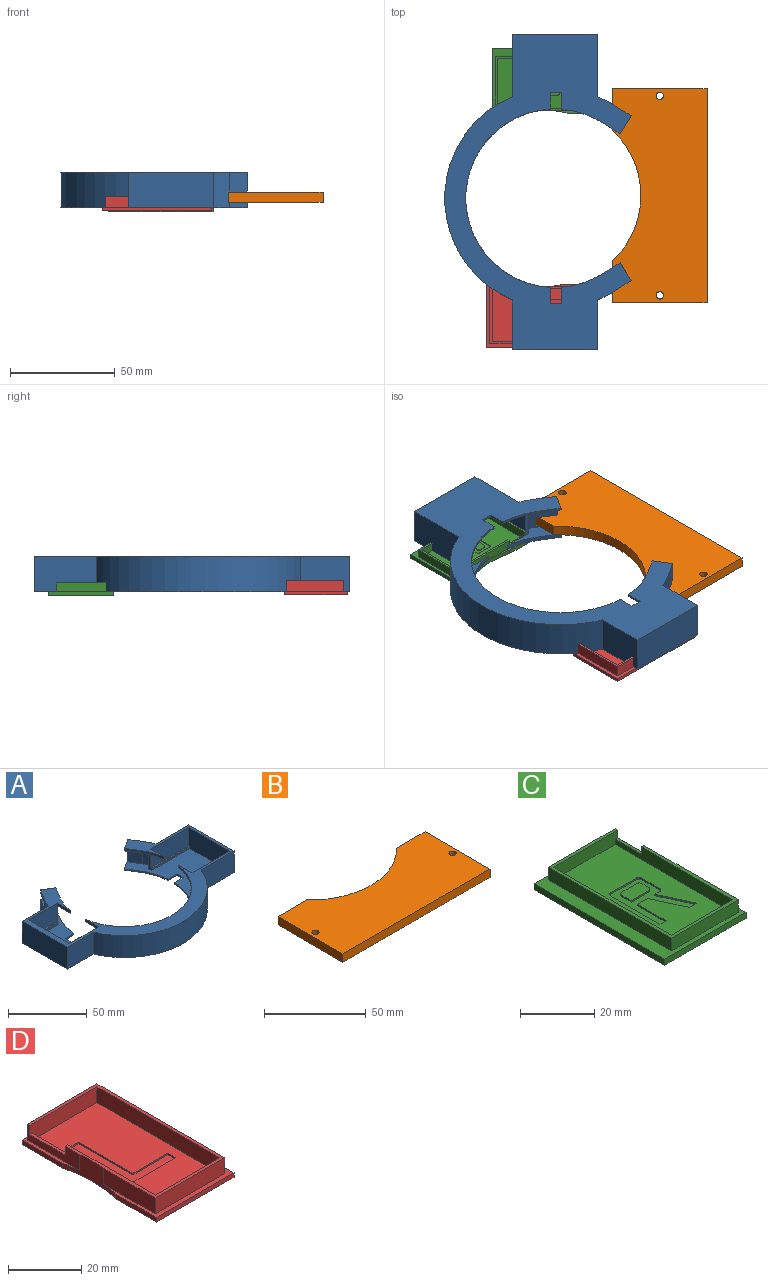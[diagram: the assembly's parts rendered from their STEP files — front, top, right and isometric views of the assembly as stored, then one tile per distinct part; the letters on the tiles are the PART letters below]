
ASSEMBLY  parts=4 mates=3
PART A: 78 faces, bbox 150x88.8x17 mm
  f0: plane 144x85.74mm, normal (0,0,1), area 3182.5mm2, adj f2,f6,f8,f10,f11,f12,f13,f14
  f1: plane 34x14.5mm, normal (0,1,0), area 493mm2, adj f18,f19,f45,f46,f75
  f2: plane 37x16mm, normal (1,0,0), area 589mm2, adj f0,f3,f18,f43,f70,f71,f72,f73
  f3: plane 26x14.5mm, normal (0,1,0), area 377mm2, adj f2,f13,f18,f42,f73
  f4: plane 8.48x5.3mm, normal (-0.85,0.53,0), area 25mm2, adj f7,f18,f24,f69
  f5: cylinder r=52.5mm len=17mm, axis (0,0,1), area 142.6mm2, adj f9,f18,f28,f39,f62,f64,f65,f66
  f6: plane 8.5x8.48mm, normal (0.85,-0.53,0), area 85mm2, adj f0,f23,f58,f67
  f7: plane 8.48x5.3mm, normal (0.53,0.85,0), area 21mm2, adj f4,f18,f25,f56,f57,f69
  f8: plane 8.5x8.48mm, normal (-0.85,-0.53,0), area 85mm2, adj f0,f10,f26,f65
  f9: plane 9.5x8.48mm, normal (0.85,0.53,0), area 95mm2, adj f5,f10,f28,f65
  f10: plane 9.5x8.48mm, normal (-0.53,0.85,0), area 27mm2, adj f0,f8,f9,f28,f59,f65
  f11: cylinder r=42.5mm len=19.27mm, axis (0,0,1), area 20.5mm2, adj f0,f28,f53,f59
  f12: cylinder r=42.5mm len=84.88mm, axis (0,0,1), area 129mm2, adj f0,f28,f49,f51
  f13: plane 14x2.75mm, normal (1,0,0), area 26mm2, adj f0,f3,f29,f31,f72,f73
  f14: plane 14x2.75mm, normal (-1,0,0), area 26mm2, adj f0,f22,f36,f47,f76,f77
  f15: cylinder r=42.5mm len=16.02mm, axis (0,0,1), area 34.4mm2, adj f18,f22,f44,f61
  f16: cylinder r=42.5mm len=19.27mm, axis (0,0,1), area 20.5mm2, adj f0,f28,f50,f54
  f17: cylinder r=42.5mm len=84mm, axis (0,0,1), area 240.9mm2, adj f18,f29,f42,f45
  f18: plane 150x88.8mm, normal (0,0,1), area 1941.9mm2, adj f1,f2,f3,f4,f5,f7,f15,f17
  f19: plane 14x2.75mm, normal (-1,0,0), area 26mm2, adj f0,f1,f29,f37,f74,f75
  f20: cylinder r=50.5mm len=92.52mm, axis (0,0,1), area 1637.7mm2, adj f0,f29,f31,f37
  f21: cylinder r=52.5mm len=96.88mm, axis (0,0,1), area 2097mm2, adj f18,f28,f34,f38
  f22: plane 28.74x15.52mm, normal (0,0,-1), area 145.9mm2, adj f14,f15,f26,f36,f44,f60,f61,f63
  f23: cylinder r=50.5mm len=14mm, axis (0,0,1), area 103.2mm2, adj f0,f6,f25,f32,f57,f68
  f24: cylinder r=52.5mm len=17mm, axis (0,0,1), area 145.1mm2, adj f4,f18,f28,f33,f55,f68
  f25: plane 28.74x15.52mm, normal (0,0,-1), area 145.9mm2, adj f7,f23,f27,f30,f32,f41,f56,f57
  f26: cylinder r=50.5mm len=14mm, axis (0,0,1), area 100.7mm2, adj f0,f8,f22,f36,f60,f64,f65,f66
  f27: cylinder r=42.5mm len=16.02mm, axis (0,0,1), area 34.4mm2, adj f18,f25,f41,f56
  f28: plane 150x88.8mm, normal (0,0,-1), area 4067.7mm2, adj f5,f9,f10,f11,f12,f16,f21,f24
  f29: plane 92.52x44mm, normal (0,0,-1), area 885mm2, adj f13,f17,f19,f20,f31,f37,f42,f45
  f30: plane 14x2.75mm, normal (1,0,0), area 26mm2, adj f0,f25,f32,f43,f70,f71
  f31: plane 14x4.26mm, normal (0,-1,0), area 59.7mm2, adj f0,f13,f20,f29
  f32: plane 14x4.26mm, normal (0,1,0), area 59.7mm2, adj f0,f23,f25,f30
  f33: plane 23.56x17mm, normal (0,1,0), area 400.6mm2, adj f18,f24,f28,f35
  f34: plane 23.56x17mm, normal (0,-1,0), area 400.6mm2, adj f18,f21,f28,f35
  f35: plane 40.5x17mm, normal (-1,0,0), area 688.5mm2, adj f18,f28,f33,f34
  f36: plane 14x4.26mm, normal (0,1,0), area 59.7mm2, adj f0,f14,f22,f26
  f37: plane 14x4.26mm, normal (0,-1,0), area 59.7mm2, adj f0,f19,f20,f29
  f38: plane 29.56x17mm, normal (0,-1,0), area 502.6mm2, adj f18,f21,f28,f40
  f39: plane 29.56x17mm, normal (0,1,0), area 502.6mm2, adj f5,f18,f28,f40
  f40: plane 40.5x17mm, normal (1,0,0), area 688.5mm2, adj f18,f28,f38,f39
  f41: plane 12x2mm, normal (-1,0,0), area 24mm2, adj f18,f25,f27,f43
  f42: plane 12x2mm, normal (-1,0,0), area 24mm2, adj f3,f17,f18,f29
  f43: plane 26x14.5mm, normal (0,-1,0), area 377mm2, adj f2,f18,f30,f41,f71
  f44: plane 12x2mm, normal (1,0,0), area 24mm2, adj f15,f18,f22,f47
  f45: plane 12x2mm, normal (1,0,0), area 24mm2, adj f1,f17,f18,f29
  f46: plane 37x16mm, normal (-1,0,0), area 589mm2, adj f0,f1,f18,f47,f74,f75,f76,f77
  f47: plane 34x14.5mm, normal (0,-1,0), area 493mm2, adj f14,f18,f44,f46,f77
  f48: plane 5.5x1mm, normal (1,0,0), area 5.5mm2, adj f0,f28,f49,f50
  f49: plane 7.78x1mm, normal (0,1,0), area 7.8mm2, adj f0,f12,f28,f48
  f50: plane 7.85x1mm, normal (0,-1,0), area 7.8mm2, adj f0,f16,f28,f48
  f51: plane 7.84x1mm, normal (0,1,0), area 7.8mm2, adj f0,f12,f28,f52
  f52: plane 5.5x1mm, normal (-1,0,0), area 5.5mm2, adj f0,f28,f51,f53
  f53: plane 7.9x1mm, normal (0,-1,0), area 7.9mm2, adj f0,f11,f28,f52
  f54: plane 8.48x5.3mm, normal (0.85,-0.53,0), area 10mm2, adj f0,f16,f28,f58
  f55: plane 9.5x8.48mm, normal (-0.85,0.53,0), area 95mm2, adj f24,f28,f58,f67
  f56: plane 8.48x5.3mm, normal (0.85,-0.53,0), area 20mm2, adj f7,f18,f25,f27
  f57: plane 8.48x5.3mm, normal (0.85,-0.53,0), area 5mm2, adj f7,f23,f25,f69
  f58: plane 9.5x8.48mm, normal (0.53,0.85,0), area 27mm2, adj f0,f6,f28,f54,f55,f67
  f59: plane 8.48x5.3mm, normal (-0.85,-0.53,0), area 10mm2, adj f0,f10,f11,f28
  f60: plane 8.48x5.3mm, normal (-0.85,-0.53,0), area 5mm2, adj f22,f26,f63,f66
  f61: plane 8.48x5.3mm, normal (-0.85,-0.53,0), area 20mm2, adj f15,f18,f22,f63
  f62: plane 8.48x5.3mm, normal (0.85,0.53,0), area 25mm2, adj f5,f18,f63,f66
  f63: plane 8.48x5.3mm, normal (-0.53,0.85,0), area 21mm2, adj f18,f22,f60,f61,f62,f66
  f64: plane 5x1.7mm, normal (-0.53,0.85,0), area 10mm2, adj f5,f26,f65,f66
  f65: plane 9.97x7.27mm, normal (0,0,1), area 21mm2, adj f5,f8,f9,f10,f26,f64
  f66: plane 9.97x7.27mm, normal (0,0,-1), area 21mm2, adj f5,f26,f60,f62,f63,f64
  f67: plane 9.54x7mm, normal (0,0,1), area 20mm2, adj f6,f55,f58,f68
  f68: plane 5x1.7mm, normal (0.53,0.85,0), area 10mm2, adj f23,f24,f67,f69
  f69: plane 9.54x7mm, normal (0,0,-1), area 20mm2, adj f4,f7,f57,f68
  f70: plane 26x1.5mm, normal (0,-1,0), area 39mm2, adj f0,f2,f30,f71
  f71: plane 26x1mm, normal (0,0,1), area 26mm2, adj f2,f30,f43,f70
  f72: plane 26x1.5mm, normal (0,1,0), area 39mm2, adj f0,f2,f13,f73
  f73: plane 26x1mm, normal (0,0,1), area 26mm2, adj f2,f3,f13,f72
  f74: plane 34x1.5mm, normal (0,1,0), area 51mm2, adj f0,f19,f46,f75
  f75: plane 34x1mm, normal (0,0,1), area 34mm2, adj f1,f19,f46,f74
  f76: plane 34x1.5mm, normal (0,-1,0), area 51mm2, adj f0,f14,f46,f77
  f77: plane 34x1mm, normal (0,0,1), area 34mm2, adj f14,f46,f47,f76
PART B: 10 faces, bbox 102x45x5 mm
  f0: plane 19.93x5mm, normal (0,1,0), area 99.7mm2, adj f2,f5,f6,f7
  f1: plane 102x5mm, normal (0,-1,0), area 510mm2, adj f2,f4,f5,f6
  f2: plane 45x5mm, normal (1,0,0), area 225mm2, adj f0,f1,f5,f6
  f3: plane 19.93x5mm, normal (0,1,0), area 99.7mm2, adj f4,f5,f6,f7
  f4: plane 45x5mm, normal (-1,0,0), area 225mm2, adj f1,f3,f5,f6
  f5: plane 102x45mm, normal (0,0,1), area 3990.9mm2, adj f0,f1,f2,f3,f4,f7,f8,f9
  f6: plane 102x45mm, normal (0,0,-1), area 3990.9mm2, adj f0,f1,f2,f3,f4,f7,f8,f9
  f7: cylinder r=42.5mm len=62.14mm, axis (0,0,1), area 348.4mm2, adj f0,f3,f5,f6
  f8: cylinder r=1.75mm len=5mm, axis (0,0,1), area 55mm2, adj f5,f6
  f9: cylinder r=1.75mm len=5mm, axis (0,0,1), area 55mm2, adj f5,f6
PART C: 42 faces, bbox 31x50x6.2 mm
  f0: plane 47x4.2mm, normal (1,0,0), area 172.4mm2, adj f3,f9,f10,f14,f16,f40,f41
  f1: plane 13.71x2mm, normal (1,0,0), area 27.4mm2, adj f3,f4,f8,f39
  f2: plane 45x23.5mm, normal (0,0,1), area 897.7mm2, adj f11,f12,f13,f14,f20,f21,f22,f23
  f3: plane 50x31mm, normal (0,0,1), area 328.8mm2, adj f0,f1,f4,f5,f6,f7,f9,f10
  f4: plane 31x2mm, normal (0,-1,0), area 62mm2, adj f1,f3,f7,f8
  f5: plane 13.71x2mm, normal (1,0,0), area 27.4mm2, adj f3,f6,f8,f39
  f6: plane 31x2mm, normal (0,1,0), area 62mm2, adj f3,f5,f7,f8
  f7: plane 50x2mm, normal (-1,0,0), area 100mm2, adj f3,f4,f6,f8
  f8: plane 50x31mm, normal (0,0,-1), area 1527.3mm2, adj f1,f4,f5,f6,f7,f39
  f9: plane 25.5x4.2mm, normal (0,-1,0), area 107.1mm2, adj f0,f3,f15,f16
  f10: plane 25.5x4.2mm, normal (0,1,0), area 107.1mm2, adj f0,f3,f15,f16
  f11: plane 45x4.2mm, normal (-1,0,0), area 164mm2, adj f2,f12,f14,f16,f40,f41
  f12: plane 23.5x4.2mm, normal (0,1,0), area 98.7mm2, adj f2,f11,f13,f16
  f13: plane 45x4.2mm, normal (1,0,0), area 189mm2, adj f2,f12,f14,f16
  f14: plane 24.5x4.2mm, normal (0,-1,0), area 101.2mm2, adj f0,f2,f11,f13,f16,f41
  f15: plane 47x4.2mm, normal (-1,0,0), area 197.4mm2, adj f3,f9,f10,f16
  f16: plane 47x25.5mm, normal (0,0,1), area 131mm2, adj f0,f9,f10,f11,f12,f13,f14,f15
  f17: plane 5.66x0.5mm, normal (0,1,0), area 2.8mm2, adj f31,f32,f33,f34
  f18: plane 2.67x0.5mm, normal (1,0,0), area 1.3mm2, adj f31,f32,f34,f35
  f19: plane 6.66x0.5mm, normal (0,-1,0), area 3.3mm2, adj f29,f31,f32,f35
  f20: plane 6.86x0.5mm, normal (-1,0,0), area 3.4mm2, adj f2,f31,f36,f37
  f21: plane 9.77x0.5mm, normal (0,-1,0), area 4.9mm2, adj f2,f31,f37,f38
  f22: plane 18.8x0.5mm, normal (1,0,0), area 9.4mm2, adj f2,f23,f31,f38
  f23: plane 2.34x0.5mm, normal (0,1,0), area 1.2mm2, adj f2,f22,f24,f31
  f24: plane 10.95x0.5mm, normal (-1,0,0), area 5.5mm2, adj f2,f23,f25,f31
  f25: plane 3.83x0.5mm, normal (0,1,0), area 1.9mm2, adj f2,f24,f26,f31
  f26: plane 10.95x4.99mm, normal (0.91,0.42,0), area 6mm2, adj f2,f25,f27,f31
  f27: plane 2.8x0.5mm, normal (0,1,0), area 1.4mm2, adj f2,f26,f28,f31
  f28: plane 10.95x4.99mm, normal (-0.91,-0.42,0), area 6mm2, adj f2,f27,f30,f31
  f29: plane 3.67x0.5mm, normal (-1,0,0), area 1.8mm2, adj f19,f31,f32,f33
  f30: plane 1.8x0.5mm, normal (0,1,0), area 0.9mm2, adj f2,f28,f31,f36
  f31: plane 19.8x13.96mm, normal (0,0,1), area 124.7mm2, adj f17,f18,f19,f20,f21,f22,f23,f24
  f32: plane 7.66x4.67mm, normal (0,0,1), area 35.1mm2, adj f17,f18,f19,f29,f33,f34,f35
  f33: cylinder r=1mm len=1mm, axis (0,0,-1), area 0.8mm2, adj f17,f29,f31,f32
  f34: cylinder r=1mm len=1mm, axis (0,0,1), area 0.8mm2, adj f17,f18,f31,f32
  f35: cylinder r=1mm len=1mm, axis (0,0,1), area 0.8mm2, adj f18,f19,f31,f32
  f36: cylinder r=1mm len=1mm, axis (0,0,-1), area 0.8mm2, adj f2,f20,f30,f31
  f37: cylinder r=1mm len=1mm, axis (0,0,-1), area 0.8mm2, adj f2,f20,f21,f31
  f38: cylinder r=1mm len=1mm, axis (0,0,1), area 0.8mm2, adj f2,f21,f22,f31
  f39: cylinder r=43.25mm len=22.58mm, axis (0,0,1), area 45.7mm2, adj f1,f3,f5,f8
  f40: plane 2.5x1mm, normal (0,1,0), area 2.5mm2, adj f0,f11,f16,f41
  f41: plane 10x1mm, normal (0,0,1), area 10mm2, adj f0,f11,f14,f40
PART D: 28 faces, bbox 30x52x6.8 mm
  f0: plane 20.4x5.3mm, normal (-1,0,0), area 66.8mm2, adj f3,f11,f15,f16,f25,f26,f27
  f1: plane 15.77x1.5mm, normal (-1,0,0), area 23.7mm2, adj f3,f4,f8,f25
  f2: plane 19.9x5.3mm, normal (-1,0,0), area 105.5mm2, adj f3,f9,f16,f25
  f3: plane 52x30mm, normal (0,0,1), area 207.9mm2, adj f0,f1,f2,f4,f5,f6,f7,f9
  f4: plane 30x1.5mm, normal (0,-1,0), area 45mm2, adj f1,f3,f5,f8
  f5: plane 52x1.5mm, normal (1,0,0), area 78mm2, adj f3,f4,f6,f8
  f6: plane 30x1.5mm, normal (0,1,0), area 45mm2, adj f3,f5,f7,f8
  f7: plane 15.77x1.5mm, normal (-1,0,0), area 23.7mm2, adj f3,f6,f8,f25
  f8: plane 52x30mm, normal (0,0,-1), area 1542.9mm2, adj f1,f4,f5,f6,f7,f25
  f9: plane 27x5.3mm, normal (0,-1,0), area 143.1mm2, adj f2,f3,f10,f16
  f10: plane 49.5x5.3mm, normal (1,0,0), area 262.3mm2, adj f3,f9,f11,f16
  f11: plane 27x5.3mm, normal (0,1,0), area 143.1mm2, adj f0,f3,f10,f16
  f12: plane 47.5x5.3mm, normal (-1,0,0), area 251.7mm2, adj f13,f15,f16,f17
  f13: plane 25x5.3mm, normal (0,1,0), area 132.5mm2, adj f12,f14,f16,f17
  f14: plane 47.5x5.3mm, normal (1,0,0), area 210.4mm2, adj f13,f15,f16,f17,f26,f27
  f15: plane 26x5.3mm, normal (0,-1,0), area 135.5mm2, adj f0,f12,f14,f16,f17,f26
  f16: plane 49.5x27mm, normal (0,0,1), area 133.7mm2, adj f0,f2,f9,f10,f11,f12,f13,f14
  f17: plane 47.5x25mm, normal (0,0,1), area 1075mm2, adj f12,f13,f14,f15,f18,f19,f20,f21
  f18: plane 3x0.5mm, normal (0,-1,0), area 1.5mm2, adj f17,f19,f23,f24
  f19: plane 24x0.5mm, normal (1,0,0), area 12mm2, adj f17,f18,f20,f24
  f20: plane 16.5x0.5mm, normal (0,1,0), area 8.3mm2, adj f17,f19,f21,f24
  f21: plane 3x0.5mm, normal (-1,0,0), area 1.5mm2, adj f17,f20,f22,f24
  f22: plane 13.5x0.5mm, normal (0,-1,0), area 6.8mm2, adj f17,f21,f23,f24
  f23: plane 21x0.5mm, normal (-1,0,0), area 10.5mm2, adj f17,f18,f22,f24
  f24: plane 24x16.5mm, normal (0,0,1), area 112.5mm2, adj f18,f19,f20,f21,f22,f23
  f25: cylinder r=42.5mm len=20.46mm, axis (0,0,1), area 79.9mm2, adj f0,f1,f2,f3,f7,f8,f16
  f26: plane 13.77x1mm, normal (0,0,1), area 13.8mm2, adj f0,f14,f15,f27
  f27: plane 3x1mm, normal (0,1,0), area 3mm2, adj f0,f14,f16,f26
PLACE A rot(axis=(0.71,0.71,0),180deg) t=(8.01,-4.48,0)mm
PLACE B rot(axis=(0,0,1),90deg) t=(57.9,-3.19,-14.5)mm
PLACE C rot(axis=(0,0,-1),90deg) t=(3.01,51.52,-19)mm
PLACE D rot(axis=(0,0,-1),90deg) t=(1.51,-60.48,-18.5)mm
MATE fastened D.f3 <-> A.f18  axis (0,0,1) through (26.51,-46.48,-17)mm
MATE fastened B.f6 <-> A.f66  axis (0,0,-1) through (80.4,47.81,-14.5)mm
MATE fastened C.f3 <-> A.f18  axis (0,0,1) through (26.51,37.52,-17)mm
